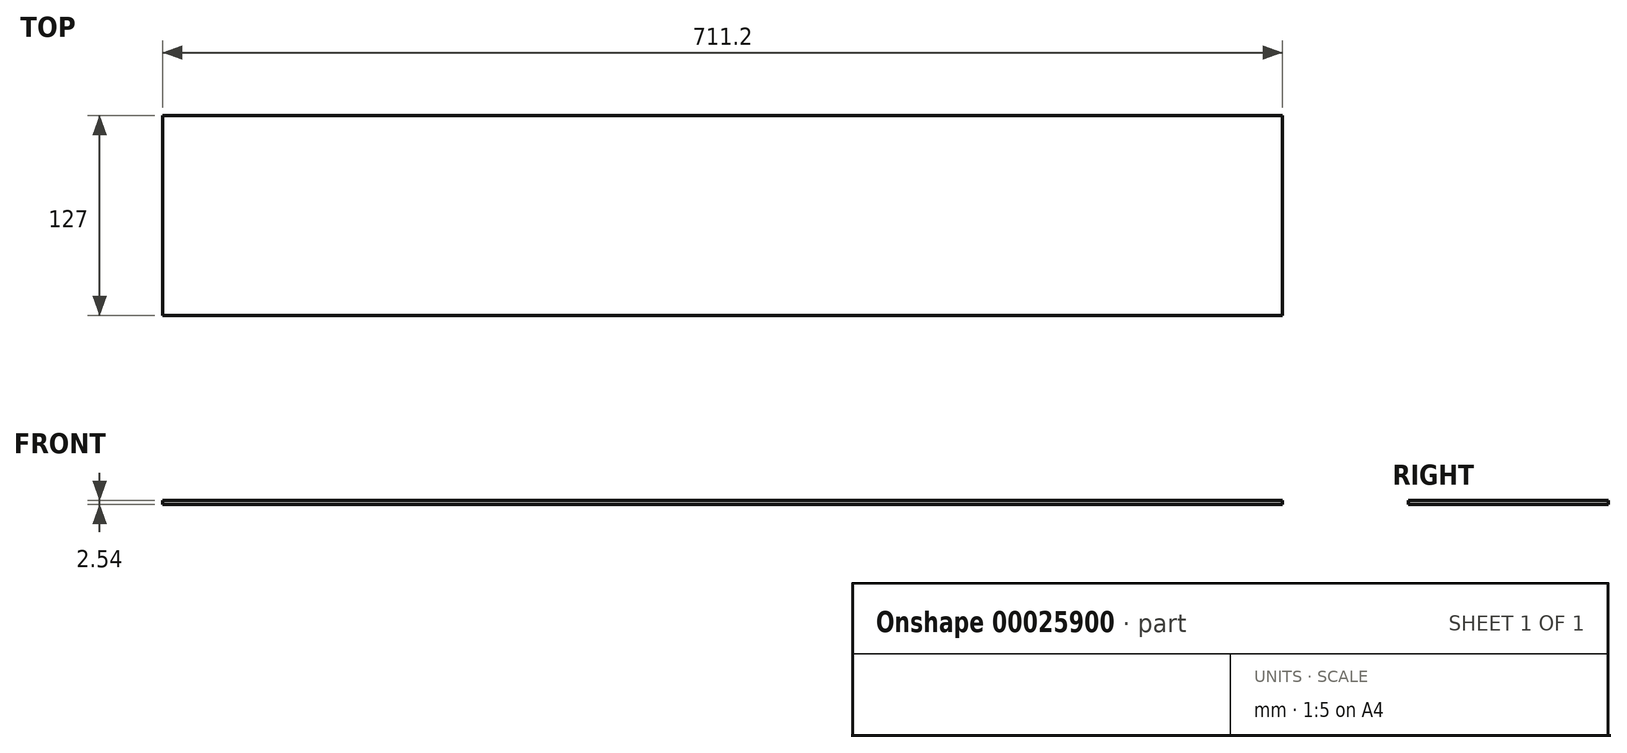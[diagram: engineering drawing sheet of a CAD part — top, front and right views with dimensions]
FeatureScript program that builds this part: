
annotation { "Feature Type Name" : "Feature", "Feature Type Description" : "" }
export const myFeature = defineFeature(function(context is Context, id is Id, definition is map)
    precondition{}
    {
        {
            var Q0;
            Q0=qCreatedBy(makeId("Top.planeOp"),FACE);
            var sketch = newSketch(context, id + "F0", { "sketchPlane" : qUnion([Q0])});
            skLineSegment(sketch, "E0.rect.bottom", {"start": v(355.6, 63.5) * mm, "end": v(-355.6, 63.5) * mm});
            skLineSegment(sketch, "E0.rect.top", {"start": v(355.6, -63.5) * mm, "end": v(-355.6, -63.5) * mm});
            skLineSegment(sketch, "E0.rect.left", {"start": v(355.6, 63.5) * mm, "end": v(355.6, -63.5) * mm});
            skLineSegment(sketch, "E0.rect.right", {"start": v(-355.6, 63.5) * mm, "end": v(-355.6, -63.5) * mm});
            skPoint(sketch, "E0.rect.middle", {"position": v(0, 0) * mm});
            skSolve(sketch);
        }
        {
            var Q0;
            Q0=makeQuery(id+"F0.imprint","IMPRINT",FACE,{"disambiguationData":[TD([[makeQuery(id+"F0.imprint","IMPRINT",EDGE,{"derivedFrom":sQuery(id+"F0.wireOp",EDGE,"E0.rect.bottom")}),1.0]])]});
            extrude(context, id + "F1", {"entities" : qUnion([Q0]), "depth" : 2.54 * mm});
        }
    });
